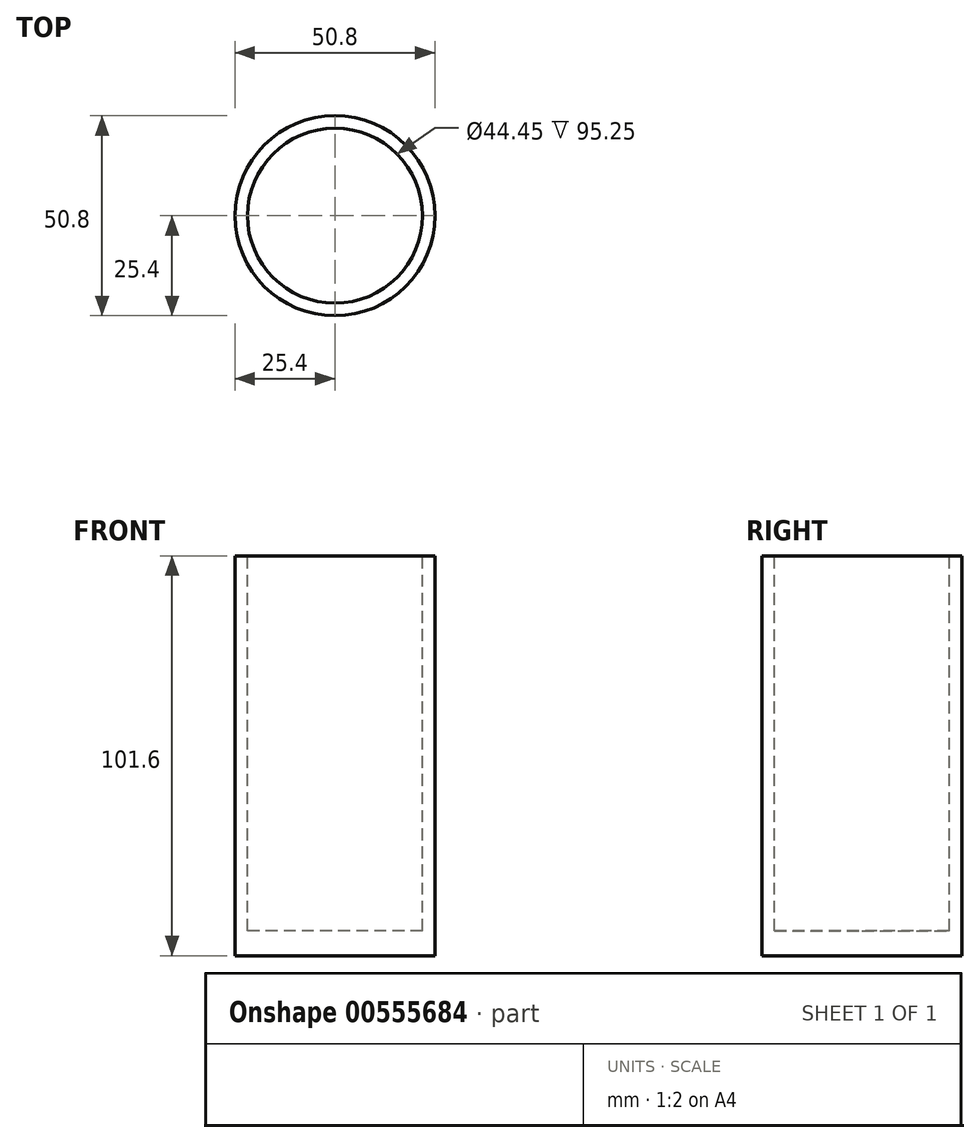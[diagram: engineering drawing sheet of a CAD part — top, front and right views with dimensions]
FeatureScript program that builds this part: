
annotation { "Feature Type Name" : "Feature", "Feature Type Description" : "" }
export const myFeature = defineFeature(function(context is Context, id is Id, definition is map)
    precondition{}
    {
        {
            var Q0;
            Q0=qCreatedBy(makeId("Top.planeOp"),FACE);
            var sketch = newSketch(context, id + "F0", { "sketchPlane" : qUnion([Q0])});
            skCircle(sketch, "E0", {"center": v(0, 0) * mm, "radius": 25.4 * mm});
            skSolve(sketch);
        }
        {
            var Q0;
            Q0=makeQuery(id+"F0.imprint","IMPRINT",FACE,{"disambiguationData":[TD([[makeQuery(id+"F0.imprint","IMPRINT",EDGE,{"derivedFrom":sQuery(id+"F0.wireOp",EDGE,"E0")}),1.0]])]});
            extrude(context, id + "F1", {"entities" : qUnion([Q0]), "depth" : 101.6 * mm});
        }
        {
            var Q0;
            Q0=makeQuery(id+"F1.opExtrude","CAP_FACE",FACE,{"disambiguationData":[OSD([sQuery(id+"F0.wireOp",EDGE,"E0")])],"isStart":false});
            var sketch = newSketch(context, id + "F2", { "sketchPlane" : qUnion([Q0])});
            skCircle(sketch, "E1", {"center": v(0, 0) * mm, "radius": 22.23 * mm});
            skSolve(sketch);
        }
        {
            var Q0;
            Q0=qSketchRegion(id+"F2",true);
            extrude(context, id + "F3", {"entities" : qUnion([Q0]), "operationType" : NewBodyOperationType.REMOVE, "oppositeDirection" : true, "depth" : 95.25 * mm});
        }
    });
